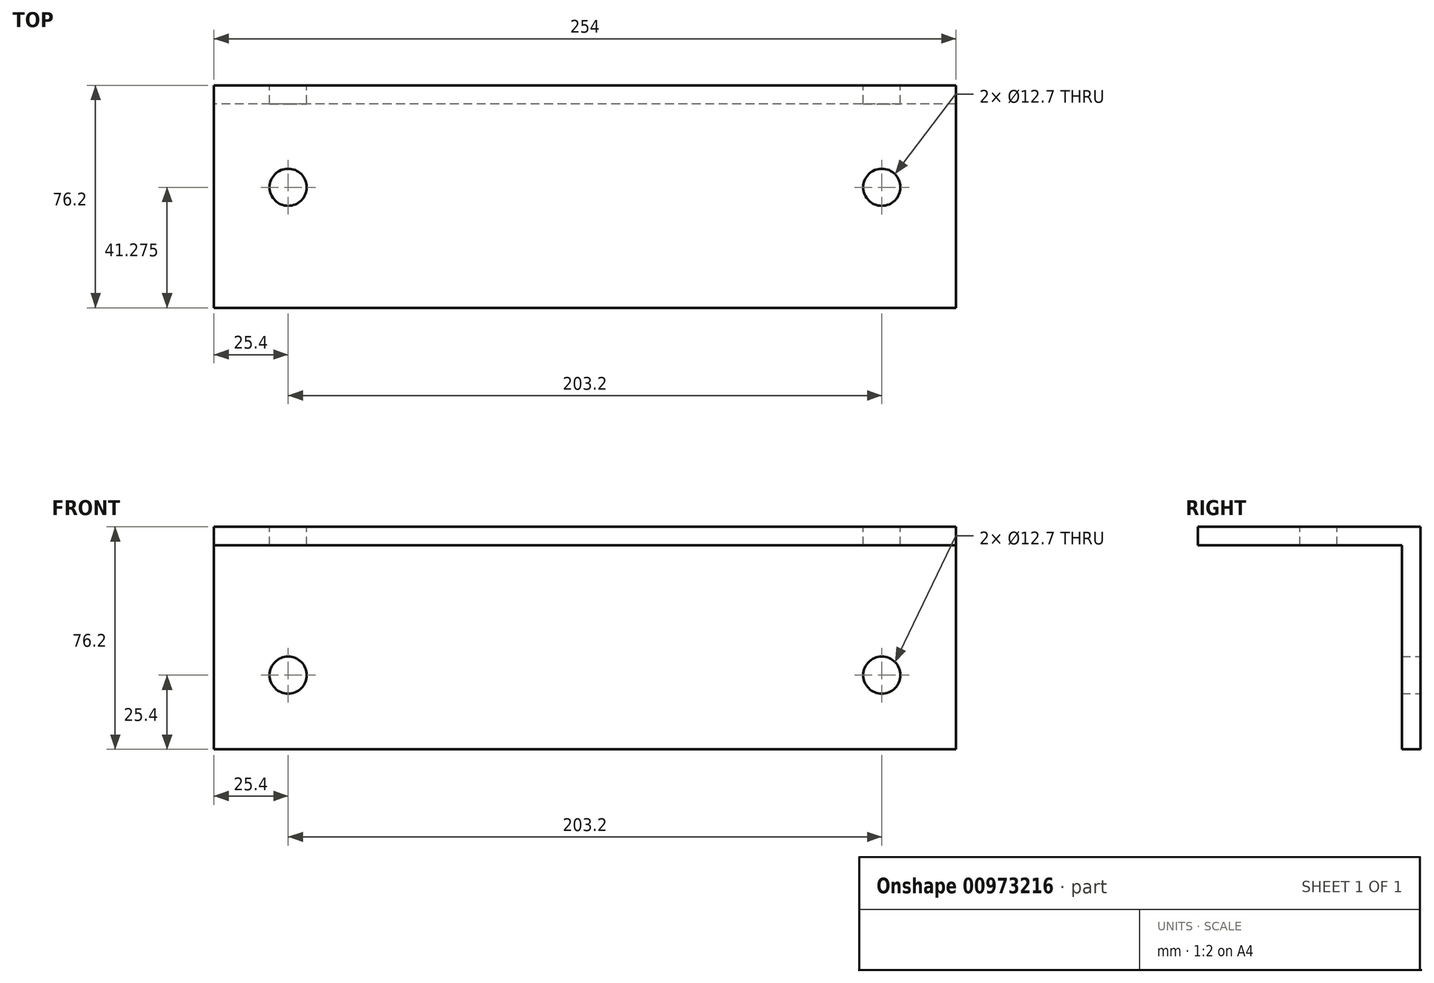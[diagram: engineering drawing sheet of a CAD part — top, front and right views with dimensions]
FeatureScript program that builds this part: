
annotation { "Feature Type Name" : "Feature", "Feature Type Description" : "" }
export const myFeature = defineFeature(function(context is Context, id is Id, definition is map)
    precondition{}
    {
        {
            var Q0;
            Q0=qCreatedBy(makeId("Right.planeOp"),FACE);
            var sketch = newSketch(context, id + "F0", { "sketchPlane" : qUnion([Q0])});
            skLineSegment(sketch, "E0.bottom", {"start": v(-38.1, 38.1) * mm, "end": v(38.1, 38.1) * mm});
            skLineSegment(sketch, "E0.top", {"start": v(-38.1, -38.1) * mm, "end": v(38.1, -38.1) * mm});
            skLineSegment(sketch, "E0.left", {"start": v(-38.1, 38.1) * mm, "end": v(-38.1, -38.1) * mm});
            skLineSegment(sketch, "E0.right", {"start": v(38.1, 38.1) * mm, "end": v(38.1, -38.1) * mm});
            skPoint(sketch, "E0.middle", {"position": v(0, 0) * mm});
            skLineSegment(sketch, "E1.0", {"start": v(31.75, 31.75) * mm, "end": v(31.75, -38.1) * mm});
            skLineSegment(sketch, "E1.1", {"start": v(-38.1, 31.75) * mm, "end": v(31.75, 31.75) * mm});
            skSolve(sketch);
        }
        {
            var Q0;
            {var subQ1=sQuery(id+"F0.wireOp",EDGE,"E0.bottom");Q0=makeQuery(id+"F0.imprint","IMPRINT",FACE,{"disambiguationData":[TD([[makeQuery(id+"F0.imprint","IMPRINT",EDGE,{"derivedFrom":subQ1}),-1.0]])]});}
            extrude(context, id + "F1", {"entities" : qUnion([Q0]), "depth" : 254 * mm, "offsetDistance" : 25.4 * mm, "symmetric" : true});
        }
        {
            var Q0;
            Q0=makeQuery(id+"F1.opExtrude","SWEPT_FACE",FACE,{"disambiguationData":[OSD([sQuery(id+"F0.wireOp",EDGE,"E0.right")])]});
            var sketch = newSketch(context, id + "F2", { "sketchPlane" : qUnion([Q0])});
            skCircle(sketch, "E2", {"center": v(-101.6, -12.7) * mm, "radius": 6.35 * mm});
            skCircle(sketch, "E3", {"center": v(101.6, -12.7) * mm, "radius": 6.35 * mm});
            skSolve(sketch);
        }
        {
            var Q0;
            Q0=makeQuery(id+"F2.imprint","IMPRINT",FACE,{"disambiguationData":[TD([[makeQuery(id+"F2.imprint","IMPRINT",EDGE,{"derivedFrom":sQuery(id+"F2.wireOp",EDGE,"E2")}),1.0]])]});
            var Q1;
            Q1=makeQuery(id+"F2.imprint","IMPRINT",FACE,{"disambiguationData":[TD([[makeQuery(id+"F2.imprint","IMPRINT",EDGE,{"derivedFrom":sQuery(id+"F2.wireOp",EDGE,"E3")}),1.0]])]});
            extrude(context, id + "F3", {"entities" : qUnion([Q0, Q1]), "operationType" : NewBodyOperationType.REMOVE, "endBound" : BoundingType.UP_TO_NEXT, "oppositeDirection" : true, "depth" : 25.4 * mm, "offsetDistance" : 25.4 * mm});
        }
        {
            var Q0;
            Q0=makeQuery(id+"F1.opExtrude","SWEPT_FACE",FACE,{"disambiguationData":[OSD([sQuery(id+"F0.wireOp",EDGE,"E0.bottom")])]});
            var sketch = newSketch(context, id + "F4", { "sketchPlane" : qUnion([Q0])});
            skCircle(sketch, "E4", {"center": v(-101.6, 3.18) * mm, "radius": 6.35 * mm});
            skCircle(sketch, "E5", {"center": v(101.6, 3.18) * mm, "radius": 6.35 * mm});
            skSolve(sketch);
        }
        {
            var Q0;
            Q0 = qSketchRegion(id + "F4", true);
            extrude(context, id + "F5", {"entities" : qUnion([Q0]), "operationType" : NewBodyOperationType.REMOVE, "endBound" : BoundingType.UP_TO_NEXT, "oppositeDirection" : true, "depth" : 25.4 * mm, "offsetDistance" : 25.4 * mm});
        }
    });
